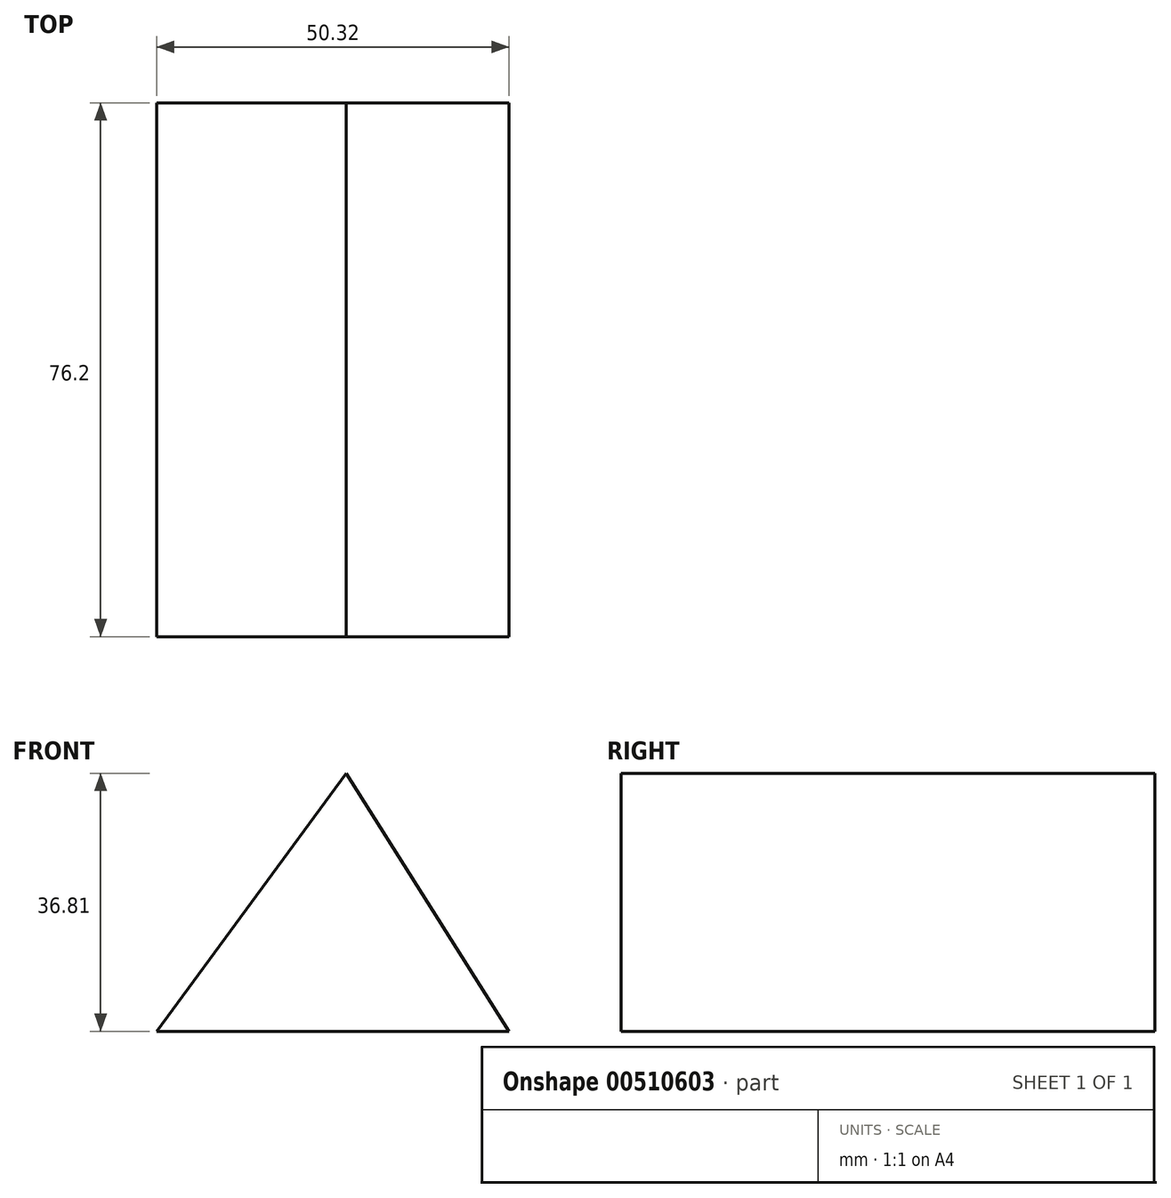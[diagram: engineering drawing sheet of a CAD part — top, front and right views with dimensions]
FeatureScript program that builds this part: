
annotation { "Feature Type Name" : "Feature", "Feature Type Description" : "" }
export const myFeature = defineFeature(function(context is Context, id is Id, definition is map)
    precondition{}
    {
        {
            var Q0;
            Q0=qCreatedBy(makeId("Front.planeOp"),FACE);
            var sketch = newSketch(context, id + "F0", { "sketchPlane" : qUnion([Q0])});
            skLineSegment(sketch, "E0", {"start": v(0, 0) * mm, "end": v(-27.02, -36.8) * mm});
            skLineSegment(sketch, "E1", {"start": v(0, 0) * mm, "end": v(23.3, -36.8) * mm});
            skLineSegment(sketch, "E2", {"start": v(-27.02, -36.8) * mm, "end": v(23.3, -36.8) * mm});
            skSolve(sketch);
        }
        {
            var Q0;
            Q0=makeQuery(id+"F0.imprint","IMPRINT",FACE,{"disambiguationData":[TD([[makeQuery(id+"F0.imprint","IMPRINT",EDGE,{"derivedFrom":sQuery(id+"F0.wireOp",EDGE,"E0")}),1.0]])]});
            extrude(context, id + "F1", {"entities" : qUnion([Q0]), "endBound" : BoundingType.SYMMETRIC, "depth" : 76.2 * mm});
        }
    });
